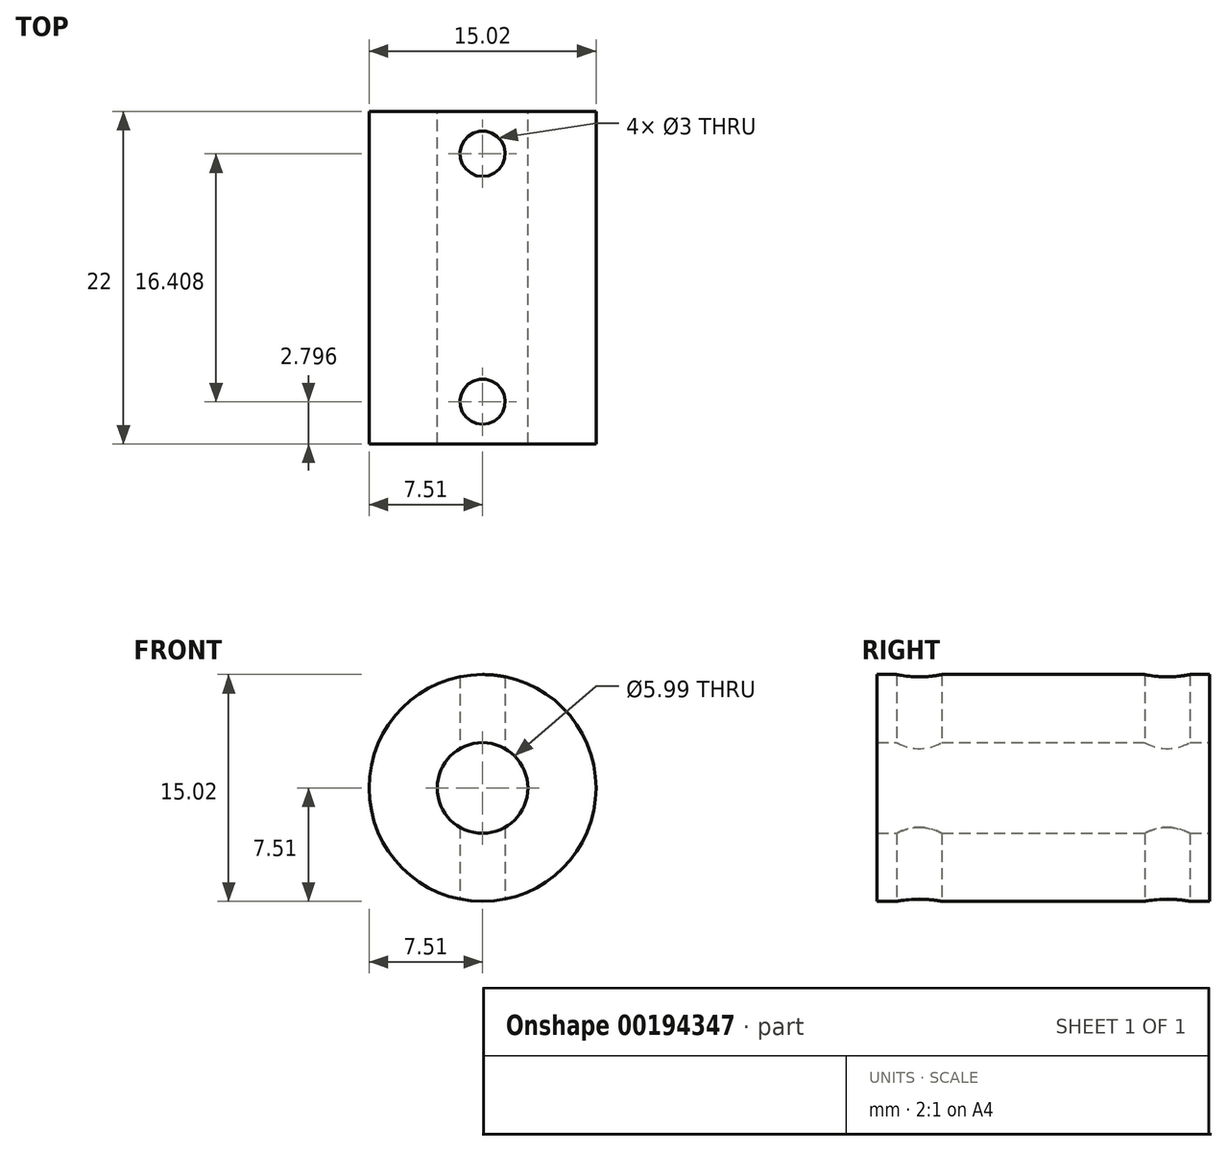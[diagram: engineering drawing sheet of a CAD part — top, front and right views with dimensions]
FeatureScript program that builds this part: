
annotation { "Feature Type Name" : "Feature", "Feature Type Description" : "" }
export const myFeature = defineFeature(function(context is Context, id is Id, definition is map)
    precondition{}
    {
        {
            var Q0;
            Q0=qCreatedBy(makeId("Front.planeOp"),FACE);
            var sketch = newSketch(context, id + "F0", { "sketchPlane" : qUnion([Q0])});
            skCircle(sketch, "E0", {"center": v(0, 0) * mm, "radius": 7.5 * mm});
            skCircle(sketch, "E1", {"center": v(0, 0) * mm, "radius": 3 * mm});
            skSolve(sketch);
        }
        {
            var Q0;
            Q0=qSketchRegion(id+"F0",true);
            extrude(context, id + "F1", {"entities" : qUnion([Q0]), "endBound" : BoundingType.SYMMETRIC, "depth" : 22 * mm});
        }
        {
            var Q0;
            Q0=qCreatedBy(makeId("Top.planeOp"),FACE);
            var sketch = newSketch(context, id + "F2", { "sketchPlane" : qUnion([Q0])});
            skCircle(sketch, "E2", {"center": v(0, 8.2) * mm, "radius": 1.5 * mm});
            skCircle(sketch, "E3", {"center": v(0, -8.2) * mm, "radius": 1.5 * mm});
            skSolve(sketch);
        }
        {
            var Q0;
            Q0=qSketchRegion(id+"F2",true);
            extrude(context, id + "F3", {"entities" : qUnion([Q0]), "operationType" : NewBodyOperationType.REMOVE, "endBound" : BoundingType.THROUGH_ALL, "depth" : 25.4 * mm, "hasSecondDirection" : true, "secondDirectionBound" : SecondDirectionBoundingType.THROUGH_ALL, "secondDirectionOppositeDirection" : true, "secondDirectionDepth" : 25.4 * mm});
        }
    });
